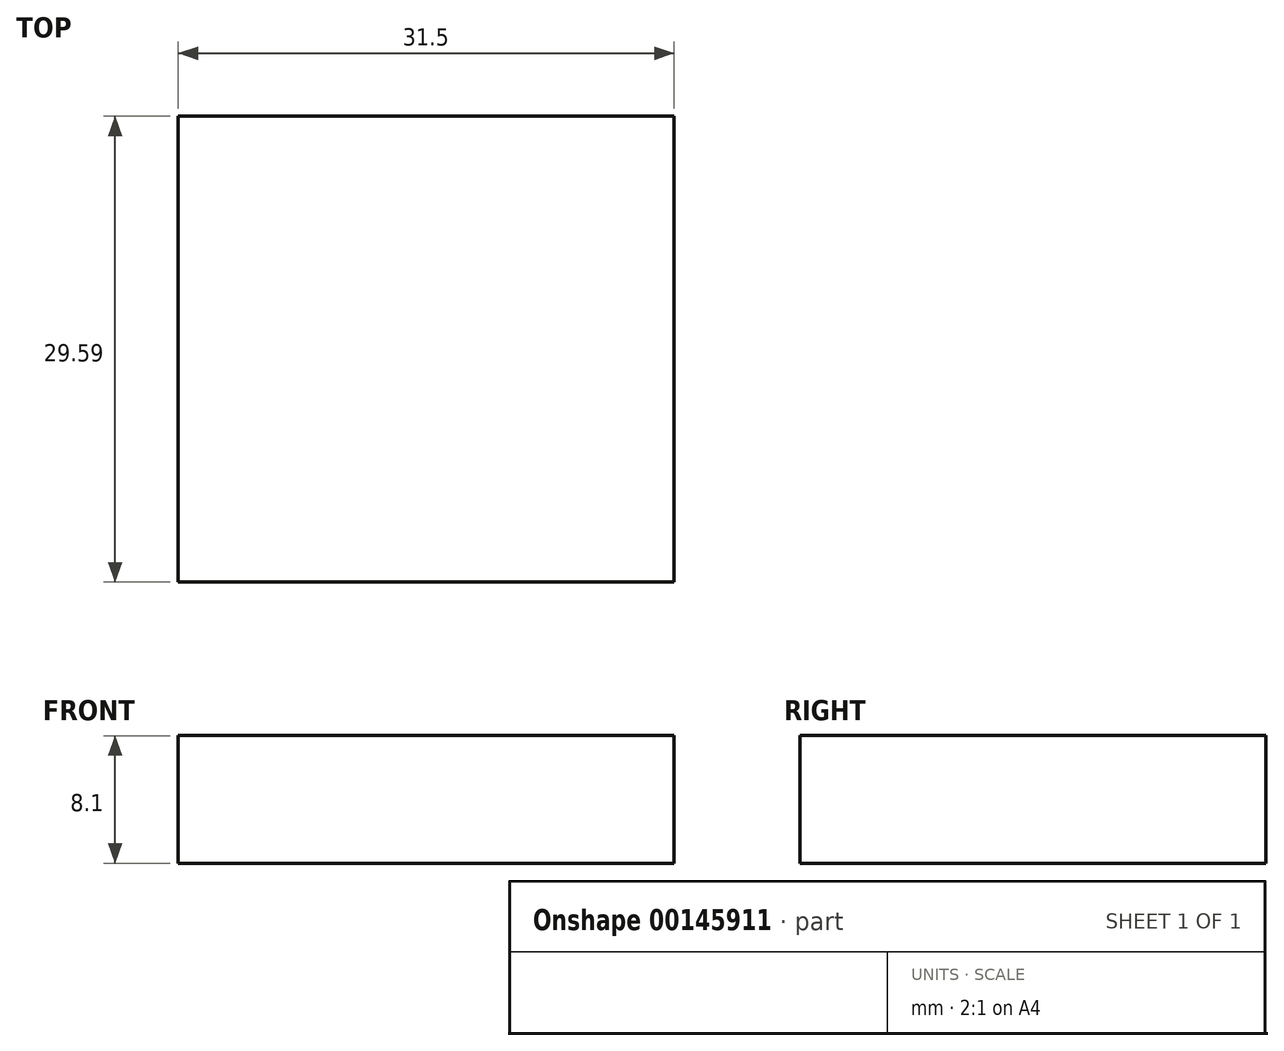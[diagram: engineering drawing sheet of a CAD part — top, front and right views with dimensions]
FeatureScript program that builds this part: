
annotation { "Feature Type Name" : "Feature", "Feature Type Description" : "" }
export const myFeature = defineFeature(function(context is Context, id is Id, definition is map)
    precondition{}
    {
        {
            var Q0;
            Q0=qCreatedBy(makeId("Top.planeOp"),FACE);
            var sketch = newSketch(context, id + "F0", { "sketchPlane" : qUnion([Q0])});
            skLineSegment(sketch, "E0.bottom", {"start": v(0, 0) * mm, "end": v(31.5, 0) * mm});
            skLineSegment(sketch, "E0.top", {"start": v(0, -29.6) * mm, "end": v(31.5, -29.6) * mm});
            skLineSegment(sketch, "E0.left", {"start": v(0, 0) * mm, "end": v(0, -29.6) * mm});
            skLineSegment(sketch, "E0.right", {"start": v(31.5, 0) * mm, "end": v(31.5, -29.6) * mm});
            skSolve(sketch);
        }
        {
            var Q0;
            Q0 = qSketchRegion(id + "F0", true);
            extrude(context, id + "F1", {"entities" : qUnion([Q0]), "depth" : 8.1 * mm});
        }
    });
